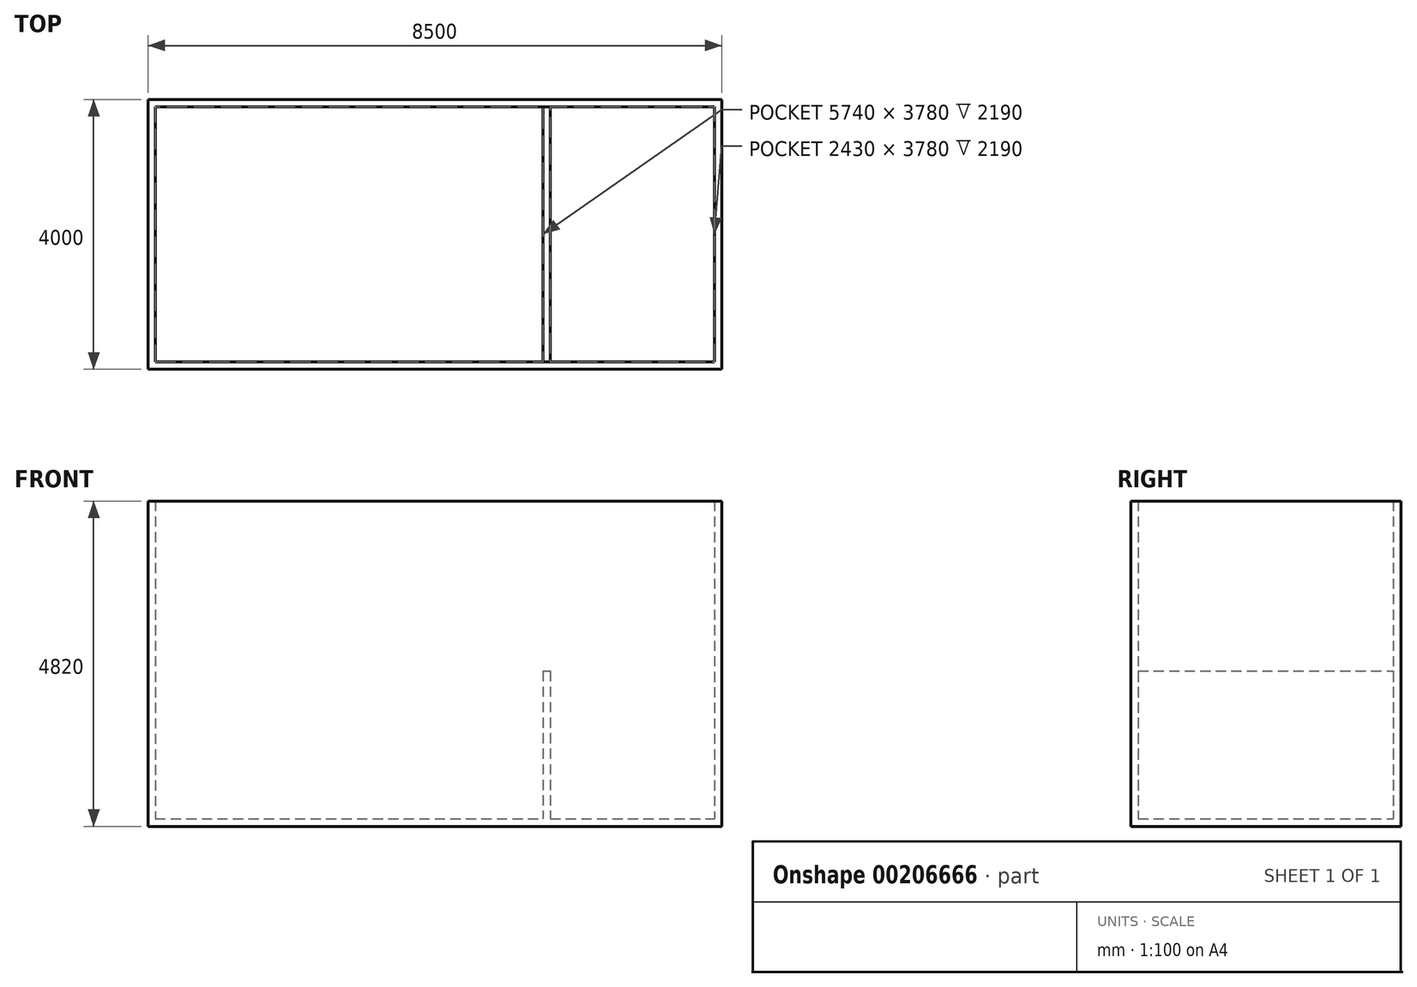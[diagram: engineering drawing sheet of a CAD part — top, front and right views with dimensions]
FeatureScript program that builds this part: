
annotation { "Feature Type Name" : "Feature", "Feature Type Description" : "" }
export const myFeature = defineFeature(function(context is Context, id is Id, definition is map)
    precondition{}
    {
        {
            var Q0;
            Q0=qCreatedBy(makeId("Top.planeOp"),FACE);
            var sketch = newSketch(context, id + "F0", { "sketchPlane" : qUnion([Q0])});
            skLineSegment(sketch, "E0.bottom", {"start": v(0, 0) * mm, "end": v(8500, 0) * mm});
            skLineSegment(sketch, "E0.top", {"start": v(0, 4000) * mm, "end": v(8500, 4000) * mm});
            skLineSegment(sketch, "E0.left", {"start": v(0, 0) * mm, "end": v(0, 4000) * mm});
            skLineSegment(sketch, "E0.right", {"start": v(8500, 0) * mm, "end": v(8500, 4000) * mm});
            skSolve(sketch);
        }
        {
            var Q0;
            Q0=makeQuery(id+"F0.imprint","IMPRINT",FACE,{"disambiguationData":[TD([[makeQuery(id+"F0.imprint","IMPRINT",EDGE,{"derivedFrom":sQuery(id+"F0.wireOp",EDGE,"E0.bottom")}),1.0]])]});
            extrude(context, id + "F1", {"entities" : qUnion([Q0]), "depth" : 4820 * mm});
        }
        {
            var Q0;
            Q0=makeQuery(id+"F1.opExtrude","CAP_FACE",FACE,{"disambiguationData":[OSD([sQuery(id+"F0.wireOp",EDGE,"E0.bottom"),sQuery(id+"F0.wireOp",EDGE,"E0.top"),sQuery(id+"F0.wireOp",EDGE,"E0.left"),sQuery(id+"F0.wireOp",EDGE,"E0.right")])],"isStart":false});
            shell(context, id + "F2", {"entities" : qUnion([Q0]), "thickness" : 110 * mm});
        }
        {
            var Q0;
            Q0=makeQuery(id+"F2.opShell","OFFSET_FACE",FACE,{"disambiguationData":[OSD([sQuery(id+"F0.wireOp",EDGE,"E0.bottom"),sQuery(id+"F0.wireOp",EDGE,"E0.top"),sQuery(id+"F0.wireOp",EDGE,"E0.left"),sQuery(id+"F0.wireOp",EDGE,"E0.right")])]});
            cPlane(context, id + "F3", {"entities" : qUnion([Q0]), "cplaneType" : CPlaneType.OFFSET, "offset" : 2300 * mm, "width" : 150 * mm, "height" : 150 * mm});
        }
        {
            var Q0;
            Q0=qCreatedBy(id+"F3.planeOp",FACE);
            var sketch = newSketch(context, id + "F4", { "sketchPlane" : qUnion([Q0])});
            skLineSegment(sketch, "E1.bottom", {"start": v(0, 0) * mm, "end": v(8450, 0) * mm});
            skLineSegment(sketch, "E1.top", {"start": v(0, 4000) * mm, "end": v(8450, 4000) * mm});
            skLineSegment(sketch, "E1.left", {"start": v(0, 0) * mm, "end": v(0, 4000) * mm});
            skLineSegment(sketch, "E1.right", {"start": v(8450, 0) * mm, "end": v(8450, 4000) * mm});
            skSolve(sketch);
        }
        {
            var Q0;
            Q0=makeQuery(id+"F2.opShell","OFFSET_FACE",FACE,{"disambiguationData":[OSD([sQuery(id+"F0.wireOp",EDGE,"E0.left")])]});
            cPlane(context, id + "F5", {"entities" : qUnion([Q0]), "cplaneType" : CPlaneType.OFFSET, "offset" : 5740 * mm, "width" : 150 * mm, "height" : 150 * mm});
        }
        {
            var Q0;
            Q0=qCreatedBy(id+"F5.planeOp",FACE);
            var sketch = newSketch(context, id + "F6", { "sketchPlane" : qUnion([Q0])});
            skLineSegment(sketch, "E2.bottom", {"start": v(0, 0) * mm, "end": v(4000, 0) * mm});
            skLineSegment(sketch, "E2.top", {"start": v(0, 2300) * mm, "end": v(4000, 2300) * mm});
            skLineSegment(sketch, "E2.left", {"start": v(0, 0) * mm, "end": v(0, 2300) * mm});
            skLineSegment(sketch, "E2.right", {"start": v(4000, 0) * mm, "end": v(4000, 2300) * mm});
            skSolve(sketch);
        }
        {
            var Q0;
            Q0 = qSketchRegion(id + "F6", true);
            extrude(context, id + "F7", {"entities" : qUnion([Q0]), "operationType" : NewBodyOperationType.ADD, "depth" : 110 * mm});
        }
    });
